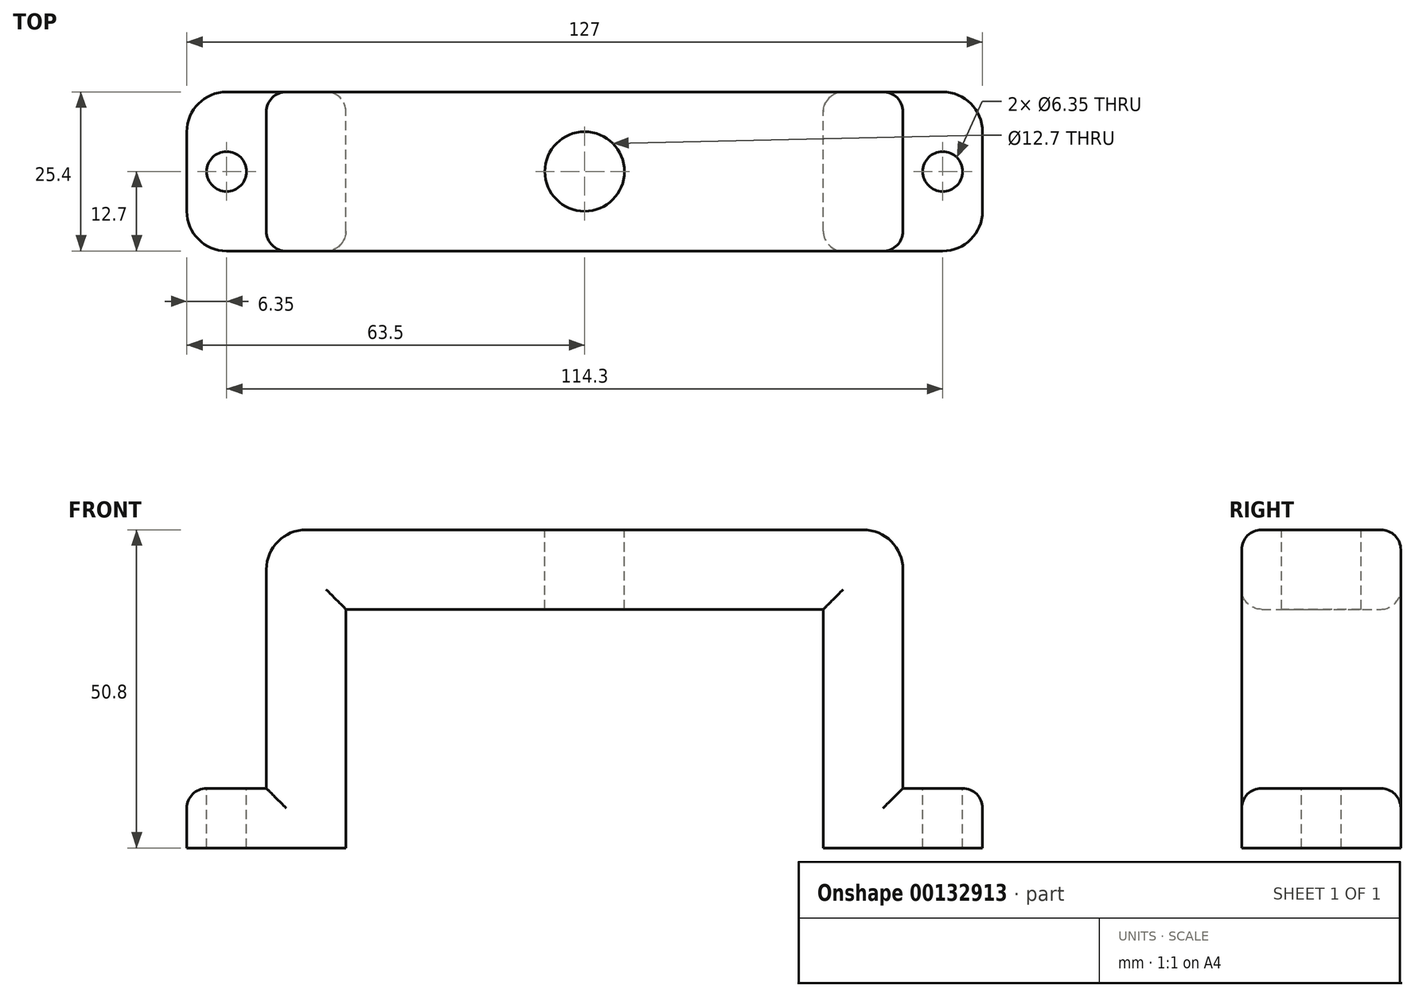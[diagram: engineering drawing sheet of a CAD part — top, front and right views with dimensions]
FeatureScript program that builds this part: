
annotation { "Feature Type Name" : "Feature", "Feature Type Description" : "" }
export const myFeature = defineFeature(function(context is Context, id is Id, definition is map)
    precondition{}
    {
        {
            var Q0;
            Q0=qCreatedBy(makeId("Front.planeOp"),FACE);
            var sketch = newSketch(context, id + "F0", { "sketchPlane" : qUnion([Q0])});
            skLineSegment(sketch, "E0", {"start": v(-63.5, -22.07) * mm, "end": v(-63.5, -31.6) * mm});
            skLineSegment(sketch, "E1", {"start": v(-63.5, -31.6) * mm, "end": v(-38.1, -31.6) * mm});
            skLineSegment(sketch, "E2", {"start": v(-38.1, -31.6) * mm, "end": v(-38.1, 6.5) * mm});
            skLineSegment(sketch, "E3", {"start": v(-38.1, 6.5) * mm, "end": v(0, 6.5) * mm});
            skLineSegment(sketch, "E4", {"start": v(-63.5, -22.07) * mm, "end": v(-50.8, -22.07) * mm});
            skLineSegment(sketch, "E5", {"start": v(-50.8, -22.07) * mm, "end": v(-50.8, 19.2) * mm});
            skLineSegment(sketch, "E6", {"start": v(-50.8, 19.2) * mm, "end": v(0, 19.2) * mm});
            skLineSegment(sketch, "E7.MirrorCS", {"start": v(50.8, 19.2) * mm, "end": v(0, 19.2) * mm});
            skLineSegment(sketch, "E8.MirrorCS", {"start": v(38.1, 6.5) * mm, "end": v(0, 6.5) * mm});
            skLineSegment(sketch, "E9.MirrorCS", {"start": v(38.1, -31.6) * mm, "end": v(38.1, 6.5) * mm});
            skLineSegment(sketch, "E10.MirrorCS", {"start": v(50.8, -22.07) * mm, "end": v(50.8, 19.2) * mm});
            skLineSegment(sketch, "E11.MirrorCS", {"start": v(63.5, -22.07) * mm, "end": v(50.8, -22.07) * mm});
            skLineSegment(sketch, "E12.MirrorCS", {"start": v(63.5, -31.6) * mm, "end": v(38.1, -31.6) * mm});
            skLineSegment(sketch, "E13.MirrorCS", {"start": v(63.5, -22.07) * mm, "end": v(63.5, -31.6) * mm});
            skSolve(sketch);
        }
        {
            var Q0;
            Q0=makeQuery(id+"F0.imprint","IMPRINT",FACE,{"disambiguationData":[TD([[makeQuery(id+"F0.imprint","IMPRINT",EDGE,{"derivedFrom":sQuery(id+"F0.wireOp",EDGE,"E0")}),1.0]])]});
            extrude(context, id + "F1", {"entities" : qUnion([Q0]), "endBound" : BoundingType.SYMMETRIC, "depth" : 25.4 * mm});
        }
        {
            var Q0;
            Q0=makeQuery(id+"F1.opExtrude","SWEPT_FACE",FACE,{"disambiguationData":[OSD([sQuery(id+"F0.wireOp",EDGE,"E4")])]});
            var sketch = newSketch(context, id + "F2", { "sketchPlane" : qUnion([Q0])});
            skCircle(sketch, "E14", {"center": v(-57.15, 0) * mm, "radius": 3.18 * mm});
            skPoint(sketch, "E14.centerSnap0", {"position": v(-50.8, 0) * mm});
            skCircle(sketch, "E15", {"center": v(57.15, 0) * mm, "radius": 3.18 * mm});
            skSolve(sketch);
        }
        {
            var Q0;
            Q0=makeQuery(id+"F2.imprint","IMPRINT",FACE,{"disambiguationData":[TD([[makeQuery(id+"F2.imprint","IMPRINT",EDGE,{"derivedFrom":sQuery(id+"F2.wireOp",EDGE,"E14")}),1.0]])]});
            var Q1;
            Q1=makeQuery(id+"F2.imprint","IMPRINT",FACE,{"disambiguationData":[TD([[makeQuery(id+"F2.imprint","IMPRINT",EDGE,{"derivedFrom":sQuery(id+"F2.wireOp",EDGE,"E15")}),1.0]])]});
            extrude(context, id + "F3", {"entities" : qUnion([Q0, Q1]), "operationType" : NewBodyOperationType.REMOVE, "endBound" : BoundingType.THROUGH_ALL, "oppositeDirection" : true, "depth" : 25.4 * mm});
        }
        {
            var Q0;
            Q0=makeQuery(id+"F1.opExtrude","SWEPT_FACE",FACE,{"disambiguationData":[OSD([sQuery(id+"F0.wireOp",EDGE,"E6"),sQuery(id+"F0.wireOp",EDGE,"E7.MirrorCS")])]});
            var sketch = newSketch(context, id + "F4", { "sketchPlane" : qUnion([Q0])});
            skCircle(sketch, "E16", {"center": v(0, 0) * mm, "radius": 6.35 * mm});
            skSolve(sketch);
        }
        {
            var Q0;
            Q0=makeQuery(id+"F4.imprint","IMPRINT",FACE,{"disambiguationData":[TD([[makeQuery(id+"F4.imprint","IMPRINT",EDGE,{"derivedFrom":sQuery(id+"F4.wireOp",EDGE,"E16")}),1.0]])]});
            extrude(context, id + "F5", {"entities" : qUnion([Q0]), "operationType" : NewBodyOperationType.REMOVE, "endBound" : BoundingType.THROUGH_ALL, "oppositeDirection" : true, "depth" : 25.4 * mm});
        }
        {
            var Q0;
            Q0=makeQuery(id+"F1.opExtrude","SWEPT_EDGE",EDGE,{"disambiguationData":[OSD([sQuery(id+"F0.wireOp",EDGE,"E5"),sQuery(id+"F0.wireOp",EDGE,"E6")])]});
            var Q1;
            Q1=makeQuery(id+"F1.opExtrude","SWEPT_EDGE",EDGE,{"disambiguationData":[OSD([sQuery(id+"F0.wireOp",EDGE,"E7.MirrorCS"),sQuery(id+"F0.wireOp",EDGE,"E10.MirrorCS")])]});
            var Q2;
            Q2=makeQuery(id+"F1.opExtrude","CAP_EDGE",EDGE,{"disambiguationData":[OSD([sQuery(id+"F0.wireOp",EDGE,"E0")])],"isStart":false});
            var Q3;
            Q3=makeQuery(id+"F1.opExtrude","CAP_EDGE",EDGE,{"disambiguationData":[OSD([sQuery(id+"F0.wireOp",EDGE,"E13.MirrorCS")])],"isStart":false});
            var Q4;
            Q4=makeQuery(id+"F1.opExtrude","CAP_EDGE",EDGE,{"disambiguationData":[OSD([sQuery(id+"F0.wireOp",EDGE,"E13.MirrorCS")])],"isStart":true});
            var Q5;
            Q5=makeQuery(id+"F1.opExtrude","CAP_EDGE",EDGE,{"disambiguationData":[OSD([sQuery(id+"F0.wireOp",EDGE,"E0")])],"isStart":true});
            fillet(context, id + "F6", {"entities" : qUnion([Q0, Q1, Q2, Q3, Q4, Q5]), "radius" : 6.35 * mm, "tangentPropagation" : true, "allowEdgeOverflow" : false});
        }
        {
            var Q0;
            Q0=makeQuery(id+"F1.opExtrude","CAP_EDGE",EDGE,{"disambiguationData":[OSD([sQuery(id+"F0.wireOp",EDGE,"E5")])],"isStart":false});
            var Q1;
            Q1=makeQuery(id+"F1.opExtrude","CAP_EDGE",EDGE,{"disambiguationData":[OSD([sQuery(id+"F0.wireOp",EDGE,"E4")])],"isStart":false});
            var Q2;
            Q2=makeQuery(id+"F1.opExtrude","CAP_EDGE",EDGE,{"disambiguationData":[OSD([sQuery(id+"F0.wireOp",EDGE,"E2")])],"isStart":false});
            var Q3;
            Q3=makeQuery(id+"F1.opExtrude","CAP_EDGE",EDGE,{"disambiguationData":[OSD([sQuery(id+"F0.wireOp",EDGE,"E3"),sQuery(id+"F0.wireOp",EDGE,"E8.MirrorCS")])],"isStart":false});
            var Q4;
            Q4=makeQuery(id+"F1.opExtrude","CAP_EDGE",EDGE,{"disambiguationData":[OSD([sQuery(id+"F0.wireOp",EDGE,"E9.MirrorCS")])],"isStart":false});
            var Q5;
            Q5=makeQuery(id+"F1.opExtrude","CAP_EDGE",EDGE,{"disambiguationData":[OSD([sQuery(id+"F0.wireOp",EDGE,"E10.MirrorCS")])],"isStart":true});
            var Q6;
            Q6=makeQuery(id+"F1.opExtrude","CAP_EDGE",EDGE,{"disambiguationData":[OSD([sQuery(id+"F0.wireOp",EDGE,"E11.MirrorCS")])],"isStart":true});
            var Q7;
            Q7=makeQuery(id+"F1.opExtrude","CAP_EDGE",EDGE,{"disambiguationData":[OSD([sQuery(id+"F0.wireOp",EDGE,"E9.MirrorCS")])],"isStart":true});
            var Q8;
            Q8=makeQuery(id+"F1.opExtrude","CAP_EDGE",EDGE,{"disambiguationData":[OSD([sQuery(id+"F0.wireOp",EDGE,"E3"),sQuery(id+"F0.wireOp",EDGE,"E8.MirrorCS")])],"isStart":true});
            var Q9;
            Q9=makeQuery(id+"F1.opExtrude","CAP_EDGE",EDGE,{"disambiguationData":[OSD([sQuery(id+"F0.wireOp",EDGE,"E2")])],"isStart":true});
            fillet(context, id + "F7", {"entities" : qUnion([Q0, Q1, Q2, Q3, Q4, Q5, Q6, Q7, Q8, Q9]), "radius" : 3.17 * mm, "tangentPropagation" : true, "allowEdgeOverflow" : false});
        }
    });
